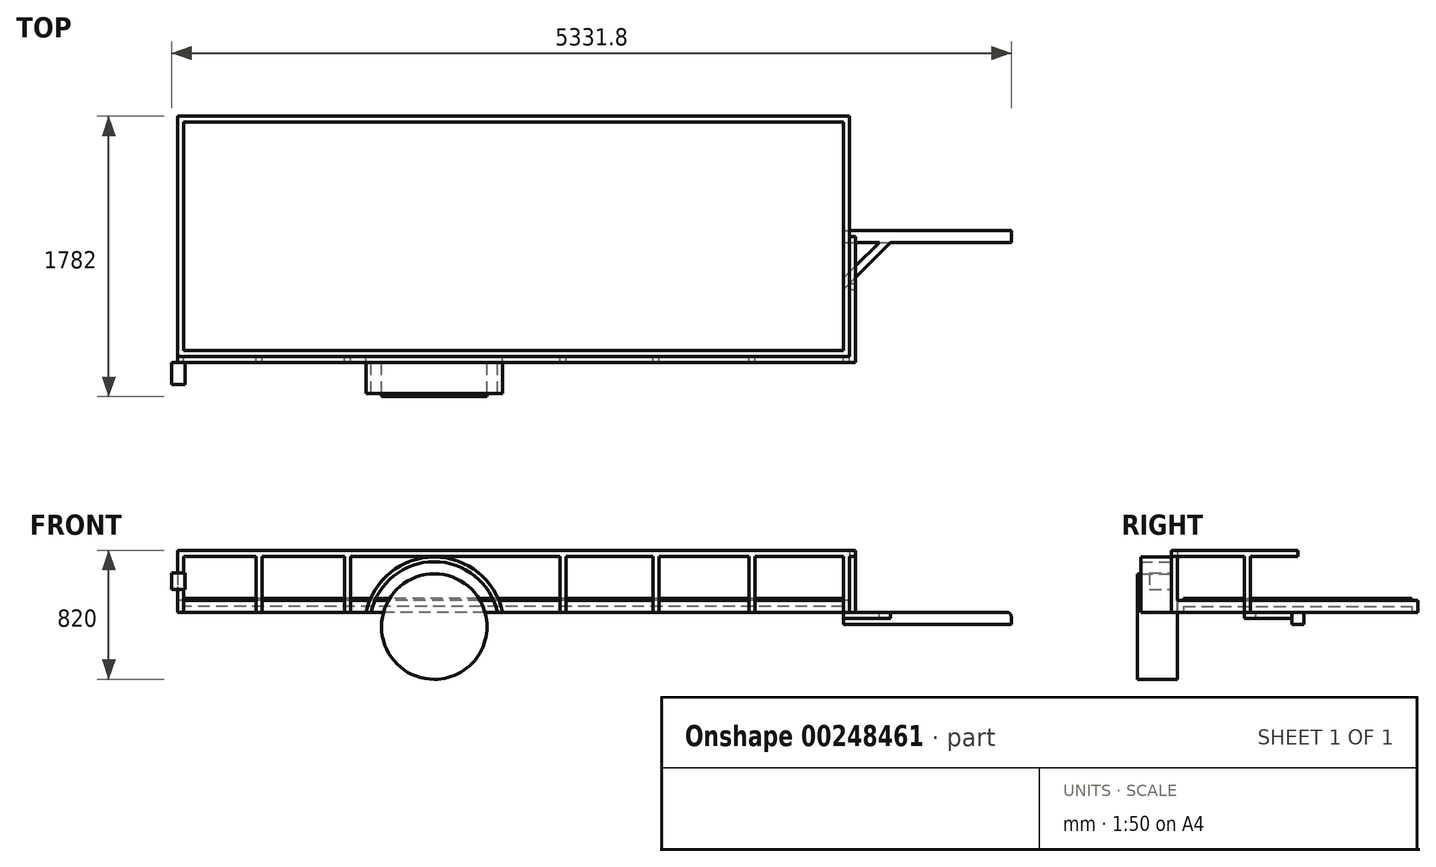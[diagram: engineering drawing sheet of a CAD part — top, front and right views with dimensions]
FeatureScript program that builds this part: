
annotation { "Feature Type Name" : "Feature", "Feature Type Description" : "" }
export const myFeature = defineFeature(function(context is Context, id is Id, definition is map)
    precondition{}
    {
        {
            var Q0;
            Q0=qCreatedBy(makeId("Top.planeOp"),FACE);
            var sketch = newSketch(context, id + "F0", { "sketchPlane" : qUnion([Q0])});
            skLineSegment(sketch, "E0.bottom", {"start": v(2133.45, -763) * mm, "end": v(-2133.45, -763) * mm});
            skLineSegment(sketch, "E0.top", {"start": v(2133.45, 763) * mm, "end": v(-2133.45, 763) * mm});
            skLineSegment(sketch, "E0.left", {"start": v(2133.45, -763) * mm, "end": v(2133.45, 763) * mm});
            skLineSegment(sketch, "E0.right", {"start": v(-2133.45, -763) * mm, "end": v(-2133.45, 763) * mm});
            skPoint(sketch, "E0.middle", {"position": v(0, 0) * mm});
            skLineSegment(sketch, "E1.0", {"start": v(2095.35, 724.9) * mm, "end": v(-2095.35, 724.9) * mm});
            skLineSegment(sketch, "E1.1", {"start": v(2095.35, -724.9) * mm, "end": v(2095.35, 724.9) * mm});
            skLineSegment(sketch, "E1.2", {"start": v(2095.35, -724.9) * mm, "end": v(-2095.35, -724.9) * mm});
            skLineSegment(sketch, "E1.3", {"start": v(-2095.35, -724.9) * mm, "end": v(-2095.35, 724.9) * mm});
            skSolve(sketch);
        }
        {
            var Q0;
            Q0 = qSketchRegion(id + "F0", true);
            extrude(context, id + "F1", {"entities" : qUnion([Q0]), "endBound" : BoundingType.SYMMETRIC, "depth" : 76.2 * mm});
        }
        {
            var Q0;
            Q0=makeQuery(id+"F0.imprint","IMPRINT",FACE,{"disambiguationData":[TD([[makeQuery(id+"F0.imprint","IMPRINT",EDGE,{"derivedFrom":sQuery(id+"F0.wireOp",EDGE,"E1.0")}),1.0]])]});
            extrude(context, id + "F2", {"entities" : qUnion([Q0]), "operationType" : NewBodyOperationType.ADD, "depth" : 50.8 * mm});
        }
        {
            var Q0;
            Q0=qCreatedBy(makeId("Front.planeOp"),FACE);
            var sketch = newSketch(context, id + "F3", { "sketchPlane" : qUnion([Q0])});
            skLineSegment(sketch, "E2.bottom", {"start": v(2095.35, -38.1) * mm, "end": v(3133.45, -38.1) * mm});
            skLineSegment(sketch, "E2.top", {"start": v(2095.35, -114.3) * mm, "end": v(3161.45, -114.3) * mm});
            skLineSegment(sketch, "E2.left", {"start": v(2095.35, -38.1) * mm, "end": v(2095.35, -114.3) * mm});
            skLineSegment(sketch, "E2.right", {"start": v(3161.45, -66.1) * mm, "end": v(3161.45, -114.3) * mm});
            skPoint(sketch, "E3.visualSharp", {"position": v(3161.45, -38.1) * mm});
            skArc(sketch, "E3.filletArc", {"start": v(3161.45, -66.1) * mm, "mid": v(3153.25, -46.3) * mm, "end": v(3133.45, -38.1) * mm});
            skSolve(sketch);
        }
        {
            var Q0;
            Q0 = qSketchRegion(id + "F3", true);
            extrude(context, id + "F4", {"entities" : qUnion([Q0]), "operationType" : NewBodyOperationType.ADD, "endBound" : BoundingType.SYMMETRIC, "depth" : 76.2 * mm});
        }
        {
            var Q0;
            Q0=makeQuery(id+"F4.opExtrude","SWEPT_FACE",FACE,{"disambiguationData":[OSD([sQuery(id+"F3.wireOp",EDGE,"E2.bottom")])]});
            var sketch = newSketch(context, id + "F5", { "sketchPlane" : qUnion([Q0])});
            skLineSegment(sketch, "E4.0", {"start": v(2323.5, -38.1) * mm, "end": v(2395.35, -38.1) * mm});
            skLineSegment(sketch, "E5.0", {"start": v(2095.35, -338.1) * mm, "end": v(2095.35, -266.26) * mm});
            skLineSegment(sketch, "E6", {"start": v(2095.35, -338.1) * mm, "end": v(2395.35, -38.1) * mm});
            skLineSegment(sketch, "E7", {"start": v(2323.5, -38.1) * mm, "end": v(2095.35, -266.26) * mm});
            skPoint(sketch, "E8.orphan", {"position": v(3133.45, -38.1) * mm});
            skPoint(sketch, "E9.orphan", {"position": v(2133.45, -38.1) * mm});
            skPoint(sketch, "E10.orphan", {"position": v(2095.35, -38.1) * mm});
            skPoint(sketch, "E11.orphan", {"position": v(2095.35, -724.9) * mm});
            skSolve(sketch);
        }
        {
            var Q0;
            Q0 = qSketchRegion(id + "F5", true);
            extrude(context, id + "F6", {"entities" : qUnion([Q0]), "operationType" : NewBodyOperationType.ADD, "oppositeDirection" : true, "depth" : 38.1 * mm});
        }
        {
            var Q0;
            {var subQ2=sQuery(id+"F0.wireOp",EDGE,"E0.bottom");var subQ3=sQuery(id+"F0.wireOp",EDGE,"E1.3");var subQ4=sQuery(id+"F0.wireOp",EDGE,"E1.2");var subQ5=sQuery(id+"F0.wireOp",EDGE,"E1.1");var subQ6=sQuery(id+"F0.wireOp",EDGE,"E1.0");var subQ7=sQuery(id+"F0.wireOp",EDGE,"E0.right");var subQ8=sQuery(id+"F0.wireOp",EDGE,"E0.top");var subQ9=sQuery(id+"F0.wireOp",EDGE,"E0.left");Q0=makeQuery(id+"F6.boolean.opBoolean","SPLIT",FACE,{"disambiguationData":[TD([makeQuery(id+"F1.opExtrude","SWEPT_FACE",FACE,{"disambiguationData":[OSD([subQ2])]})])],"derivedFrom":makeQuery(id+"F1.opExtrude","CAP_FACE",FACE,{"disambiguationData":[OSD([subQ2,subQ8,subQ9,subQ7,subQ6,subQ5,subQ4,subQ3])],"isStart":true})});}
            var sketch = newSketch(context, id + "F7", { "sketchPlane" : qUnion([Q0])});
            skLineSegment(sketch, "E12.bottom", {"start": v(-2133.45, 801.1) * mm, "end": v(-2095.35, 801.1) * mm});
            skLineSegment(sketch, "E12.top", {"start": v(-2133.45, 763) * mm, "end": v(-2095.35, 763) * mm});
            skLineSegment(sketch, "E12.left", {"start": v(-2133.45, 801.1) * mm, "end": v(-2133.45, 763) * mm});
            skLineSegment(sketch, "E12.right", {"start": v(-2095.35, 801.1) * mm, "end": v(-2095.35, 763) * mm});
            skLineSegment(sketch, "E13.bottom", {"start": v(-1633.45, 801.1) * mm, "end": v(-1595.35, 801.1) * mm});
            skLineSegment(sketch, "E13.top", {"start": v(-1633.45, 763) * mm, "end": v(-1595.35, 763) * mm});
            skLineSegment(sketch, "E13.left", {"start": v(-1633.45, 801.1) * mm, "end": v(-1633.45, 763) * mm});
            skLineSegment(sketch, "E13.right", {"start": v(-1595.35, 801.1) * mm, "end": v(-1595.35, 763) * mm});
            skLineSegment(sketch, "E14.bottom", {"start": v(-1073.45, 801.1) * mm, "end": v(-1035.35, 801.1) * mm});
            skLineSegment(sketch, "E14.top", {"start": v(-1073.45, 763) * mm, "end": v(-1035.35, 763) * mm});
            skLineSegment(sketch, "E14.left", {"start": v(-1073.45, 801.1) * mm, "end": v(-1073.45, 763) * mm});
            skLineSegment(sketch, "E14.right", {"start": v(-1035.35, 801.1) * mm, "end": v(-1035.35, 763) * mm});
            skLineSegment(sketch, "E15.bottom", {"start": v(296.55, 801.1) * mm, "end": v(334.65, 801.1) * mm});
            skLineSegment(sketch, "E15.top", {"start": v(296.55, 763) * mm, "end": v(334.65, 763) * mm});
            skLineSegment(sketch, "E15.left", {"start": v(296.55, 801.1) * mm, "end": v(296.55, 763) * mm});
            skLineSegment(sketch, "E15.right", {"start": v(334.65, 801.1) * mm, "end": v(334.65, 763) * mm});
            skLineSegment(sketch, "E16.bottom", {"start": v(886.55, 801.1) * mm, "end": v(924.65, 801.1) * mm});
            skLineSegment(sketch, "E16.top", {"start": v(886.55, 763) * mm, "end": v(924.65, 763) * mm});
            skLineSegment(sketch, "E16.left", {"start": v(886.55, 801.1) * mm, "end": v(886.55, 763) * mm});
            skLineSegment(sketch, "E16.right", {"start": v(924.65, 801.1) * mm, "end": v(924.65, 763) * mm});
            skLineSegment(sketch, "E17.bottom", {"start": v(1496.55, 801.1) * mm, "end": v(1534.65, 801.1) * mm});
            skLineSegment(sketch, "E17.top", {"start": v(1496.55, 763) * mm, "end": v(1534.65, 763) * mm});
            skLineSegment(sketch, "E17.left", {"start": v(1496.55, 801.1) * mm, "end": v(1496.55, 763) * mm});
            skLineSegment(sketch, "E17.right", {"start": v(1534.65, 801.1) * mm, "end": v(1534.65, 763) * mm});
            skLineSegment(sketch, "E18.bottom", {"start": v(2095.35, 801.1) * mm, "end": v(2133.45, 801.1) * mm});
            skLineSegment(sketch, "E18.top", {"start": v(2095.35, 763) * mm, "end": v(2133.45, 763) * mm});
            skLineSegment(sketch, "E18.left", {"start": v(2095.35, 801.1) * mm, "end": v(2095.35, 763) * mm});
            skLineSegment(sketch, "E18.right", {"start": v(2133.45, 801.1) * mm, "end": v(2133.45, 763) * mm});
            skLineSegment(sketch, "E19.bottom", {"start": v(2133.45, 338.1) * mm, "end": v(2171.55, 338.1) * mm});
            skLineSegment(sketch, "E19.top", {"start": v(2133.45, 300) * mm, "end": v(2171.55, 300) * mm});
            skLineSegment(sketch, "E19.left", {"start": v(2133.45, 338.1) * mm, "end": v(2133.45, 300) * mm});
            skLineSegment(sketch, "E19.right", {"start": v(2171.55, 338.1) * mm, "end": v(2171.55, 300) * mm});
            skSolve(sketch);
        }
        {
            var Q0;
            Q0 = qSketchRegion(id + "F7", true);
            extrude(context, id + "F8", {"entities" : qUnion([Q0]), "operationType" : NewBodyOperationType.ADD, "oppositeDirection" : true, "depth" : 394 * mm});
        }
        {
            var Q0;
            Q0=makeQuery(id+"F8.opExtrude","CAP_FACE",FACE,{"disambiguationData":[OSD([sQuery(id+"F7.wireOp",EDGE,"E12.bottom"),sQuery(id+"F7.wireOp",EDGE,"E12.top"),sQuery(id+"F7.wireOp",EDGE,"E12.left"),sQuery(id+"F7.wireOp",EDGE,"E12.right")])],"isStart":false});
            var sketch = newSketch(context, id + "F9", { "sketchPlane" : qUnion([Q0])});
            skLineSegment(sketch, "E20.0", {"start": v(2133.45, -763) * mm, "end": v(-2133.45, -763) * mm});
            skLineSegment(sketch, "E21.0", {"start": v(-2133.45, -801.1) * mm, "end": v(-2133.45, -763) * mm});
            skLineSegment(sketch, "E22.0", {"start": v(-2133.45, -801.1) * mm, "end": v(2171.55, -801.1) * mm});
            skLineSegment(sketch, "E23.0", {"start": v(2171.55, -801.1) * mm, "end": v(2171.55, 0) * mm});
            skLineSegment(sketch, "E24.0", {"start": v(2133.45, -763) * mm, "end": v(2133.45, 0) * mm});
            skPoint(sketch, "E25.orphan", {"position": v(-2095.35, -801.1) * mm});
            skPoint(sketch, "E26.orphan", {"position": v(2171.55, -338.1) * mm});
            skPoint(sketch, "E27.orphan", {"position": v(2133.45, -338.1) * mm});
            skPoint(sketch, "E28.orphan", {"position": v(-2095.35, -763) * mm});
            skLineSegment(sketch, "E29", {"start": v(2133.45, 0) * mm, "end": v(2171.55, 0) * mm});
            skPoint(sketch, "E30.orphan", {"position": v(2171.55, -300) * mm});
            skPoint(sketch, "E31.orphan", {"position": v(2133.45, -300) * mm});
            skSolve(sketch);
        }
        {
            var Q0;
            Q0 = qSketchRegion(id + "F9", true);
            extrude(context, id + "F10", {"entities" : qUnion([Q0]), "operationType" : NewBodyOperationType.ADD, "oppositeDirection" : true, "depth" : 38.1 * mm});
        }
        {
            var Q0;
            Q0=makeQuery(id+"F10.boolean.opBoolean","MERGE",FACE,{"derivedFrom":[makeQuery(id+"F8.opExtrude","SWEPT_FACE",FACE,{"disambiguationData":[OSD([sQuery(id+"F7.wireOp",EDGE,"E12.bottom")])]}),makeQuery(id+"F8.opExtrude","SWEPT_FACE",FACE,{"disambiguationData":[OSD([sQuery(id+"F7.wireOp",EDGE,"E13.bottom")])]}),makeQuery(id+"F8.opExtrude","SWEPT_FACE",FACE,{"disambiguationData":[OSD([sQuery(id+"F7.wireOp",EDGE,"E14.bottom")])]}),makeQuery(id+"F8.opExtrude","SWEPT_FACE",FACE,{"disambiguationData":[OSD([sQuery(id+"F7.wireOp",EDGE,"E15.bottom")])]}),makeQuery(id+"F8.opExtrude","SWEPT_FACE",FACE,{"disambiguationData":[OSD([sQuery(id+"F7.wireOp",EDGE,"E16.bottom")])]}),makeQuery(id+"F8.opExtrude","SWEPT_FACE",FACE,{"disambiguationData":[OSD([sQuery(id+"F7.wireOp",EDGE,"E17.bottom")])]}),makeQuery(id+"F8.opExtrude","SWEPT_FACE",FACE,{"disambiguationData":[OSD([sQuery(id+"F7.wireOp",EDGE,"E18.bottom")])]}),makeQuery(id+"F10.opExtrude","SWEPT_FACE",FACE,{"disambiguationData":[OSD([sQuery(id+"F9.wireOp",EDGE,"E22.0")])]})]});
            var sketch = newSketch(context, id + "F11", { "sketchPlane" : qUnion([Q0])});
            skLineSegment(sketch, "E32.bottom", {"start": v(-2085.35, 211.9) * mm, "end": v(-2170.35, 211.9) * mm});
            skLineSegment(sketch, "E32.top", {"start": v(-2085.35, 106.9) * mm, "end": v(-2170.35, 106.9) * mm});
            skLineSegment(sketch, "E32.left", {"start": v(-2085.35, 211.9) * mm, "end": v(-2085.35, 106.9) * mm});
            skLineSegment(sketch, "E32.right", {"start": v(-2170.35, 211.9) * mm, "end": v(-2170.35, 106.9) * mm});
            skSolve(sketch);
        }
        {
            var Q0;
            Q0 = qSketchRegion(id + "F11", true);
            extrude(context, id + "F12", {"entities" : qUnion([Q0]), "operationType" : NewBodyOperationType.ADD, "depth" : 140 * mm});
        }
        {
            var Q0;
            {var subQ8=sQuery(id+"F0.wireOp",EDGE,"E0.bottom");var subQ10=sQuery(id+"F7.wireOp",EDGE,"E14.right");Q0=makeQuery(id+"F8.boolean.opBoolean","SPLIT",FACE,{"disambiguationData":[TD([makeQuery(id+"F8.opExtrude","SWEPT_FACE",FACE,{"disambiguationData":[OSD([subQ10])]})])],"derivedFrom":makeQuery(id+"F1.opExtrude","SWEPT_FACE",FACE,{"disambiguationData":[OSD([subQ8])]})});}
            var sketch = newSketch(context, id + "F13", { "sketchPlane" : qUnion([Q0])});
            skCircle(sketch, "E33", {"center": v(-503.45, -129.1) * mm, "radius": 335 * mm});
            skSolve(sketch);
        }
        {
            var Q0;
            Q0 = qSketchRegion(id + "F13", true);
            extrude(context, id + "F14", {"entities" : qUnion([Q0]), "operationType" : NewBodyOperationType.ADD, "depth" : 256 * mm});
        }
        {
            var Q0;
            {var subQ3=sQuery(id+"F7.wireOp",EDGE,"E14.right");var subQ4=makeQuery(id+"F8.opExtrude","SWEPT_FACE",FACE,{"disambiguationData":[OSD([subQ3])]});var subQ17=sQuery(id+"F0.wireOp",EDGE,"E0.bottom");Q0=makeQuery(id+"F14.boolean.opBoolean","SPLIT",FACE,{"disambiguationData":[TD([subQ4])],"derivedFrom":makeQuery(id+"F8.boolean.opBoolean","SPLIT",FACE,{"disambiguationData":[TD([subQ4])],"derivedFrom":makeQuery(id+"F1.opExtrude","SWEPT_FACE",FACE,{"disambiguationData":[OSD([subQ17])]})})});}
            var sketch = newSketch(context, id + "F15", { "sketchPlane" : qUnion([Q0])});
            skArc(sketch, "E34", {"start": v(-71.02, -38.1) * mm, "mid": v(-503.45, 312.8) * mm, "end": v(-935.88, -38.1) * mm});
            skArc(sketch, "E35", {"start": v(-101.73, -38.1) * mm, "mid": v(-503.45, 282.8) * mm, "end": v(-905.17, -38.1) * mm});
            skLineSegment(sketch, "E36.0", {"start": v(-905.17, -38.1) * mm, "end": v(-935.88, -38.1) * mm});
            skPoint(sketch, "E37.orphan", {"position": v(296.55, -38.1) * mm});
            skPoint(sketch, "E38.orphan", {"position": v(-181.05, -38.1) * mm});
            skPoint(sketch, "E39.orphan", {"position": v(-825.85, -38.1) * mm});
            skPoint(sketch, "E40.orphan", {"position": v(-1035.35, -38.1) * mm});
            skLineSegment(sketch, "E41.0", {"start": v(-71.02, -38.1) * mm, "end": v(-101.73, -38.1) * mm});
            skSolve(sketch);
        }
        {
            var Q0;
            Q0 = qSketchRegion(id + "F15", true);
            extrude(context, id + "F16", {"entities" : qUnion([Q0]), "operationType" : NewBodyOperationType.ADD, "depth" : 234 * mm});
        }
    });
